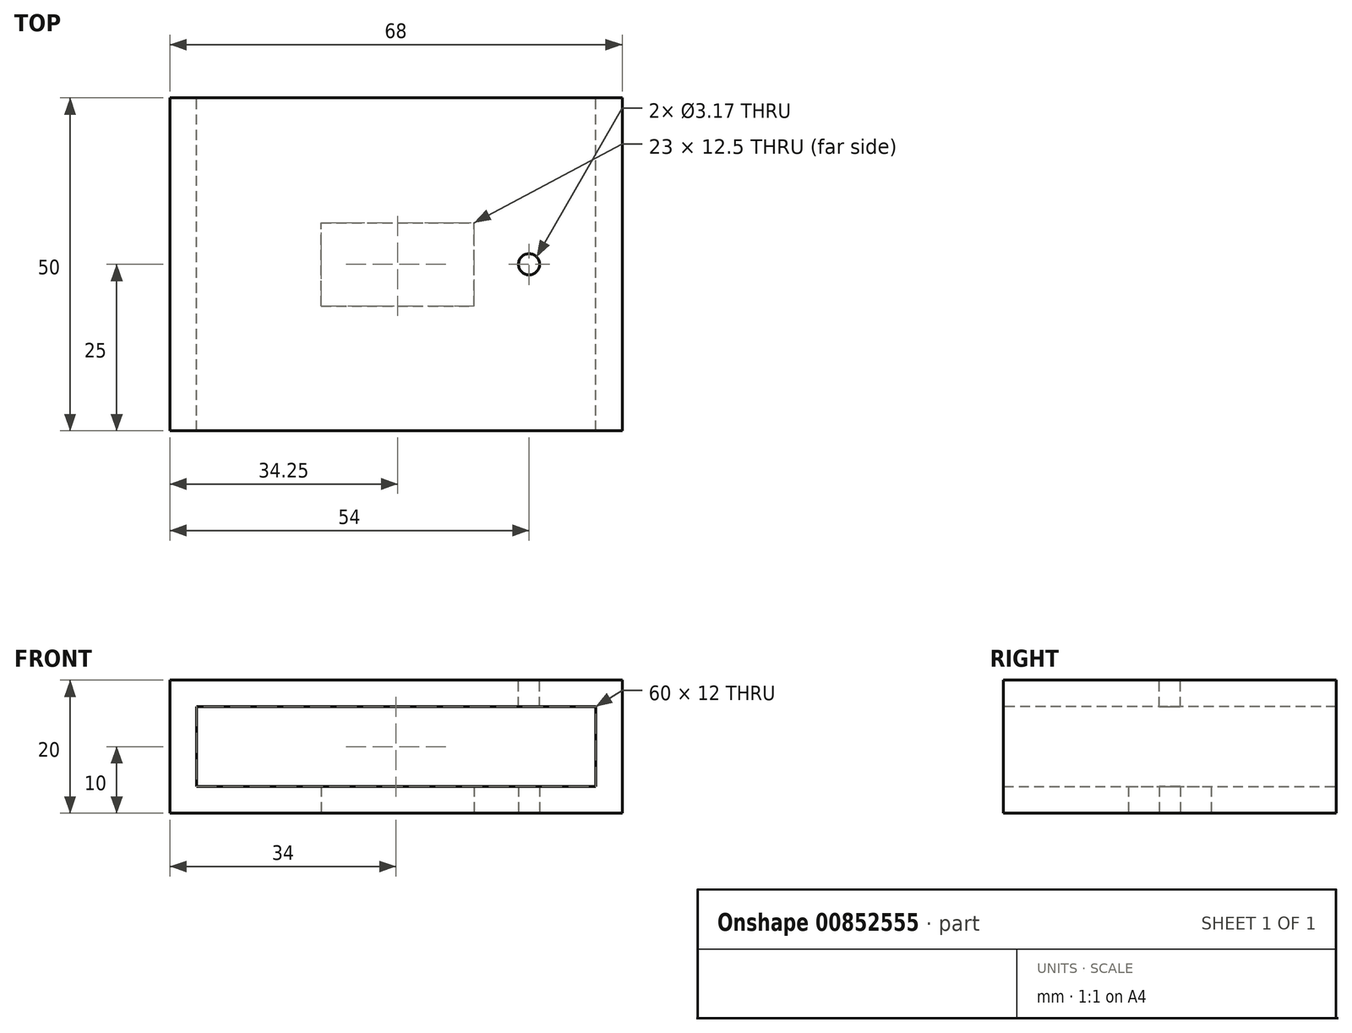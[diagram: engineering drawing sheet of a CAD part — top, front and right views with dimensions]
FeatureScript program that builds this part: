
annotation { "Feature Type Name" : "Feature", "Feature Type Description" : "" }
export const myFeature = defineFeature(function(context is Context, id is Id, definition is map)
    precondition{}
    {
        {
            var Q0;
            Q0=qCreatedBy(makeId("Top.planeOp"),FACE);
            var sketch = newSketch(context, id + "F0", { "sketchPlane" : qUnion([Q0])});
            skLineSegment(sketch, "E0.bottom", {"start": v(34, -25) * mm, "end": v(-34, -25) * mm});
            skLineSegment(sketch, "E0.top", {"start": v(34, 25) * mm, "end": v(-34, 25) * mm});
            skLineSegment(sketch, "E0.left", {"start": v(34, -25) * mm, "end": v(34, 25) * mm});
            skLineSegment(sketch, "E0.right", {"start": v(-34, -25) * mm, "end": v(-34, 25) * mm});
            skPoint(sketch, "E0.middle", {"position": v(0, 0) * mm});
            skLineSegment(sketch, "E1.bottom", {"start": v(30, -25) * mm, "end": v(-30, -25) * mm});
            skLineSegment(sketch, "E1.top", {"start": v(30, 25) * mm, "end": v(-30, 25) * mm});
            skLineSegment(sketch, "E1.left", {"start": v(30, -25) * mm, "end": v(30, 25) * mm});
            skLineSegment(sketch, "E1.right", {"start": v(-30, -25) * mm, "end": v(-30, 25) * mm});
            skCircle(sketch, "E2", {"center": v(20, 0) * mm, "radius": 1.59 * mm});
            skLineSegment(sketch, "E3.bottom", {"start": v(-11.25, -6.25) * mm, "end": v(11.75, -6.25) * mm});
            skLineSegment(sketch, "E3.top", {"start": v(-11.25, 6.25) * mm, "end": v(11.75, 6.25) * mm});
            skLineSegment(sketch, "E3.left", {"start": v(-11.25, -6.25) * mm, "end": v(-11.25, 6.25) * mm});
            skLineSegment(sketch, "E3.right", {"start": v(11.75, -6.25) * mm, "end": v(11.75, 6.25) * mm});
            skSolve(sketch);
        }
        {
            var Q0;
            {var subQ1=sQuery(id+"F0.wireOp",EDGE,"E1.left");Q0=makeQuery(id+"F0.imprint","IMPRINT",FACE,{"disambiguationData":[TD([[makeQuery(id+"F0.imprint","IMPRINT",EDGE,{"derivedFrom":subQ1}),1.0]])]});}
            extrude(context, id + "F1", {"entities" : qUnion([Q0]), "depth" : 4 * mm, "offsetDistance" : 25 * mm});
        }
        {
            var Q0;
            {var subQ0=sQuery(id+"F0.wireOp",EDGE,"E0.right");Q0=makeQuery(id+"F0.imprint","IMPRINT",FACE,{"disambiguationData":[TD([[makeQuery(id+"F0.imprint","IMPRINT",EDGE,{"derivedFrom":subQ0}),-1.0]])]});}
            var Q1;
            {var subQ2=sQuery(id+"F0.wireOp",EDGE,"E0.left");Q1=makeQuery(id+"F0.imprint","IMPRINT",FACE,{"disambiguationData":[TD([[makeQuery(id+"F0.imprint","IMPRINT",EDGE,{"derivedFrom":subQ2}),1.0]])]});}
            extrude(context, id + "F2", {"entities" : qUnion([Q0, Q1]), "operationType" : NewBodyOperationType.ADD, "depth" : 20 * mm, "offsetDistance" : 25 * mm});
        }
        {
            var Q0;
            Q0=qCreatedBy(makeId("Top.planeOp"),FACE);
            cPlane(context, id + "F3", {"entities" : qUnion([Q0]), "cplaneType" : CPlaneType.OFFSET, "offset" : 20 * mm, "width" : 150 * mm, "height" : 150 * mm});
        }
        {
            var Q0;
            Q0=qCreatedBy(id+"F3.planeOp",FACE);
            var sketch = newSketch(context, id + "F4", { "sketchPlane" : qUnion([Q0])});
            skLineSegment(sketch, "E4.bottom", {"start": v(30, 25) * mm, "end": v(-30, 25) * mm});
            skLineSegment(sketch, "E4.top", {"start": v(30, -25) * mm, "end": v(-30, -25) * mm});
            skLineSegment(sketch, "E4.left", {"start": v(30, 25) * mm, "end": v(30, -25) * mm});
            skLineSegment(sketch, "E4.right", {"start": v(-30, 25) * mm, "end": v(-30, -25) * mm});
            skPoint(sketch, "E4.middle", {"position": v(0, 0) * mm});
            skCircle(sketch, "E5", {"center": v(20, 0) * mm, "radius": 1.59 * mm});
            skSolve(sketch);
        }
        {
            var Q0;
            Q0=makeQuery(id+"F4.imprint","IMPRINT",FACE,{"disambiguationData":[TD([[makeQuery(id+"F4.imprint","IMPRINT",EDGE,{"derivedFrom":sQuery(id+"F4.wireOp",EDGE,"E4.bottom")}),1.0]])]});
            extrude(context, id + "F5", {"entities" : qUnion([Q0]), "operationType" : NewBodyOperationType.ADD, "oppositeDirection" : true, "depth" : 4 * mm, "offsetDistance" : 25 * mm});
        }
    });
